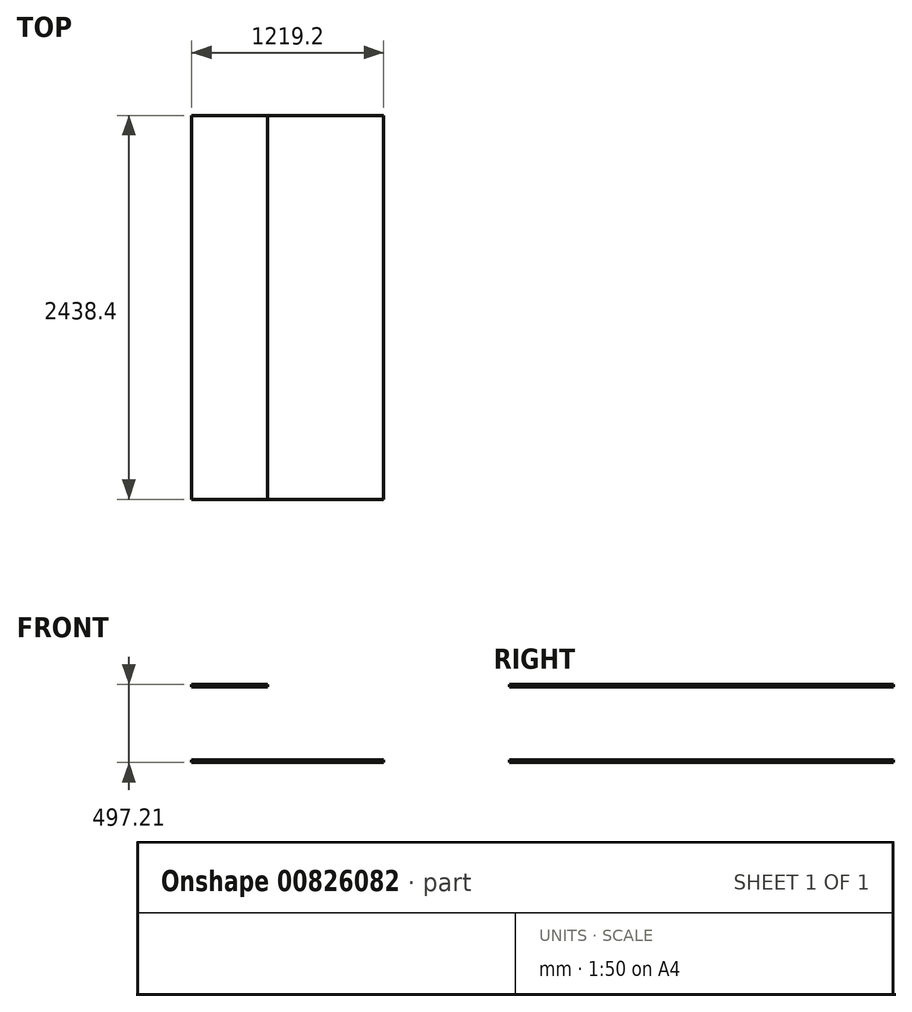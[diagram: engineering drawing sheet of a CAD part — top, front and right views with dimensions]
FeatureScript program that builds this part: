
annotation { "Feature Type Name" : "Feature", "Feature Type Description" : "" }
export const myFeature = defineFeature(function(context is Context, id is Id, definition is map)
    precondition{}
    {
        {
            var Q0;
            Q0=qCreatedBy(makeId("Top.planeOp"),FACE);
            var sketch = newSketch(context, id + "F0", { "sketchPlane" : qUnion([Q0])});
            skLineSegment(sketch, "E0.bottom", {"start": v(0, 0) * mm, "end": v(1219.2, 0) * mm});
            skLineSegment(sketch, "E0.top", {"start": v(0, 2438.4) * mm, "end": v(1219.2, 2438.4) * mm});
            skLineSegment(sketch, "E0.left", {"start": v(0, 0) * mm, "end": v(0, 2438.4) * mm});
            skLineSegment(sketch, "E0.right", {"start": v(1219.2, 0) * mm, "end": v(1219.2, 2438.4) * mm});
            skSolve(sketch);
        }
        {
            var Q0;
            Q0=qSketchRegion(id+"F0",true);
            extrude(context, id + "F1", {"entities" : qUnion([Q0]), "depth" : 15.88 * mm, "offsetDistance" : 25.4 * mm});
        }
        {
            var Q0;
            Q0=qCreatedBy(makeId("Front.planeOp"),FACE);
            var sketch = newSketch(context, id + "F2", { "sketchPlane" : qUnion([Q0])});
            skLineSegment(sketch, "E1.bottom", {"start": v(0, 481.34) * mm, "end": v(482.6, 481.34) * mm});
            skLineSegment(sketch, "E1.top", {"start": v(0, 497.21) * mm, "end": v(482.6, 497.21) * mm});
            skLineSegment(sketch, "E1.left", {"start": v(0, 481.34) * mm, "end": v(0, 497.21) * mm});
            skLineSegment(sketch, "E1.right", {"start": v(482.6, 481.34) * mm, "end": v(482.6, 497.21) * mm});
            skSolve(sketch);
        }
        {
            var Q0;
            Q0=qSketchRegion(id+"F2",true);
            extrude(context, id + "F3", {"entities" : qUnion([Q0]), "oppositeDirection" : true, "depth" : 2438.4 * mm, "offsetDistance" : 25.4 * mm});
        }
    });
